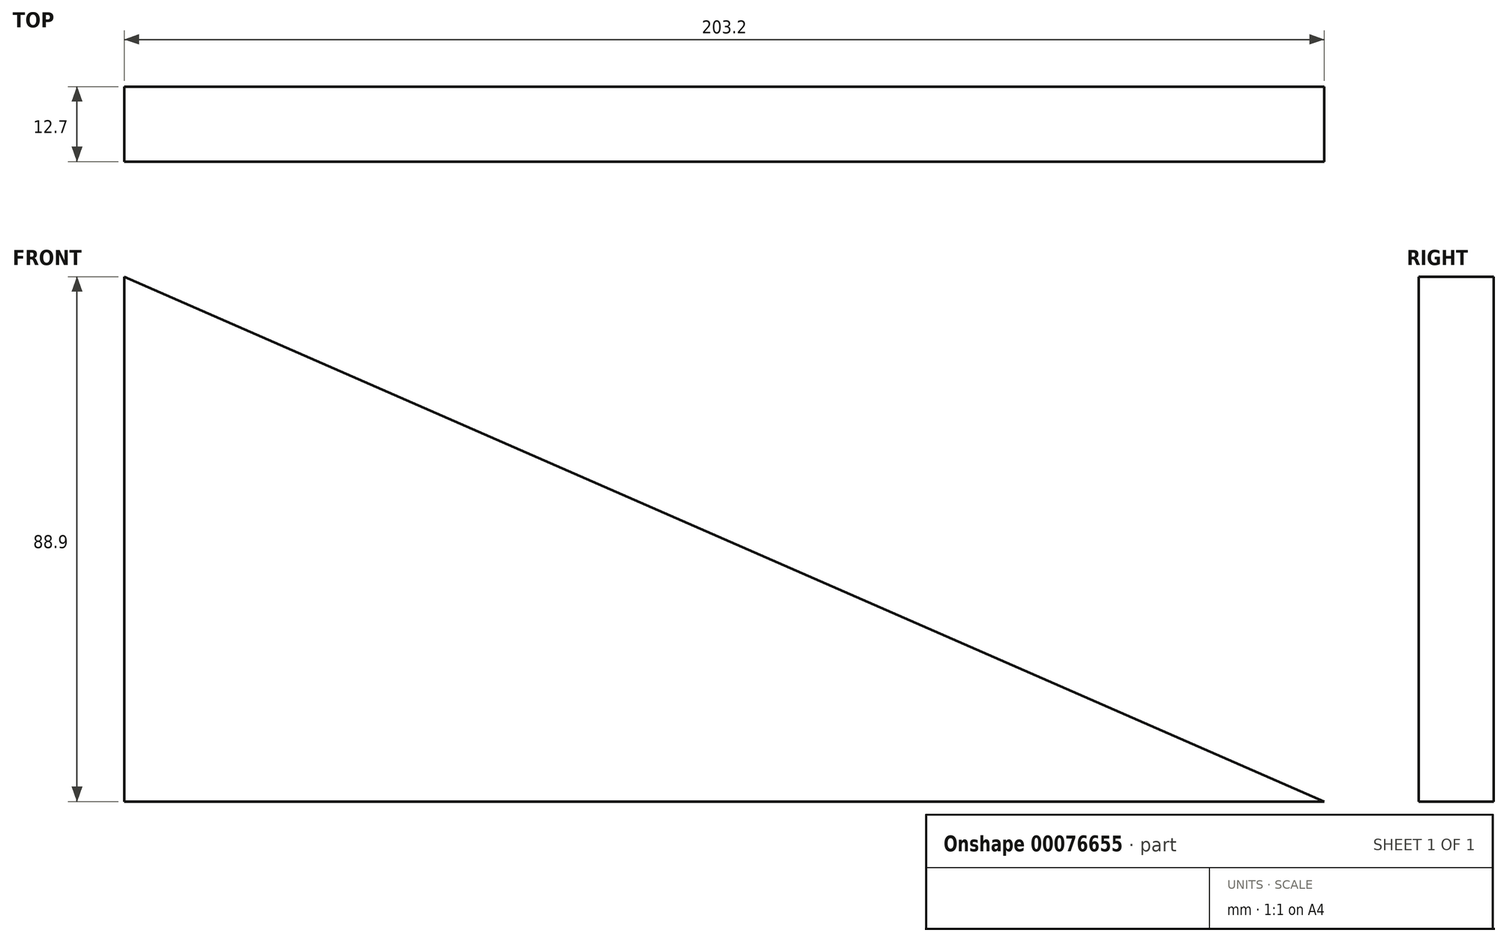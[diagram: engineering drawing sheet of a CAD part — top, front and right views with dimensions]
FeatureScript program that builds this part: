
annotation { "Feature Type Name" : "Feature", "Feature Type Description" : "" }
export const myFeature = defineFeature(function(context is Context, id is Id, definition is map)
    precondition{}
    {
        {
            var Q0;
            Q0=qCreatedBy(makeId("Front.planeOp"),FACE);
            var sketch = newSketch(context, id + "F0", { "sketchPlane" : qUnion([Q0])});
            skLineSegment(sketch, "E0", {"start": v(0, 0) * mm, "end": v(0, 88.9) * mm});
            skLineSegment(sketch, "E1", {"start": v(0, 88.9) * mm, "end": v(203.2, 0) * mm});
            skLineSegment(sketch, "E2", {"start": v(203.2, 0) * mm, "end": v(0, 0) * mm});
            skSolve(sketch);
        }
        {
            var Q0;
            Q0=makeQuery(id+"F0.imprint","IMPRINT",FACE,{"disambiguationData":[TD([[makeQuery(id+"F0.imprint","IMPRINT",EDGE,{"derivedFrom":sQuery(id+"F0.wireOp",EDGE,"E0")}),-1.0]])]});
            extrude(context, id + "F1", {"entities" : qUnion([Q0]), "depth" : 12.7 * mm});
        }
    });
